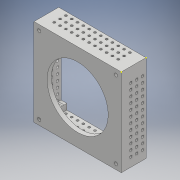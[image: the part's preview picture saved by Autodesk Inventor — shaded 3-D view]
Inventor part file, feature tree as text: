
AUTODESK INVENTOR PART (.ipt)
format: ipt  version: 2018 (Build 220112000, 112)  size: 640,000 bytes
history: native  units: mm
features: sketch x9, extrude x7, pattern_linear x4
ambient origin geometry x8: Origin, YZ Plane, XZ Plane, XY Plane, X Axis, Y Axis, Z Axis, Center Point
bodies: Solid1 (feature_tree)
feature tree (20):
  sketch  "Sketch1"  dims[d0=150.0mm d1=150.0mm]
  extrude  "Extrusion1"  Depth=150.0mm
  extrude  "Extrusion2"  Depth=7.5mm TaperAngle=0.0deg
  extrude  "Extrusion3"  Depth=35.0mm TaperAngle=0.0deg
  extrude  "Extrusion4"  Depth=10.0mm
  pattern_linear  "Rectangular Pattern1"  Count1=2 Spacing1=132.0mm
  extrude  "Extrusion5"  Depth=132.0mm
  pattern_linear  "Rectangular Pattern2"  Count1=8 Spacing1=0.0mm
  extrude  "Extrusion6"  Depth=132.0mm
  pattern_linear  "Rectangular Pattern3"  Count1=30 Spacing1=0.0mm
  extrude  "Extrusion7"  Depth=10.0mm
  pattern_linear  "Rectangular Pattern4"  Count1=30 Spacing1=0.0mm
  sketch  "Sketch9"  dims[d39=120.0mm d41=10.0mm d42=30.0mm d44=10.0mm]
  sketch  "Sketch2"  dims[d2=7.5mm d3=0.0mm d5=7.5mm d6=0.0mm]
  sketch  "Sketch3"  dims[d7=4.0mm d8=35.0mm d9=0.0mm]
  sketch  "Sketch4"  dims[d10=10.0mm d11=10.0mm]
  sketch  "Sketch5"  dims[d12=35.0mm d13=0.0mm d14=20.0mm d16=132.0mm]
  sketch  "Sketch6"  dims[d17=20.0mm d19=132.0mm d20=5.5mm d21=80.0mm d22=0.0mm]
  sketch  "Sketch7"  dims[d23=20.0mm d25=132.0mm d26=20.0mm d28=132.0mm d29=300.0mm d30=0.0mm]
  sketch  "Sketch8"  dims[d31=120.0mm d33=10.0mm d34=30.0mm d36=10.0mm d37=300.0mm d38=0.0mm]
